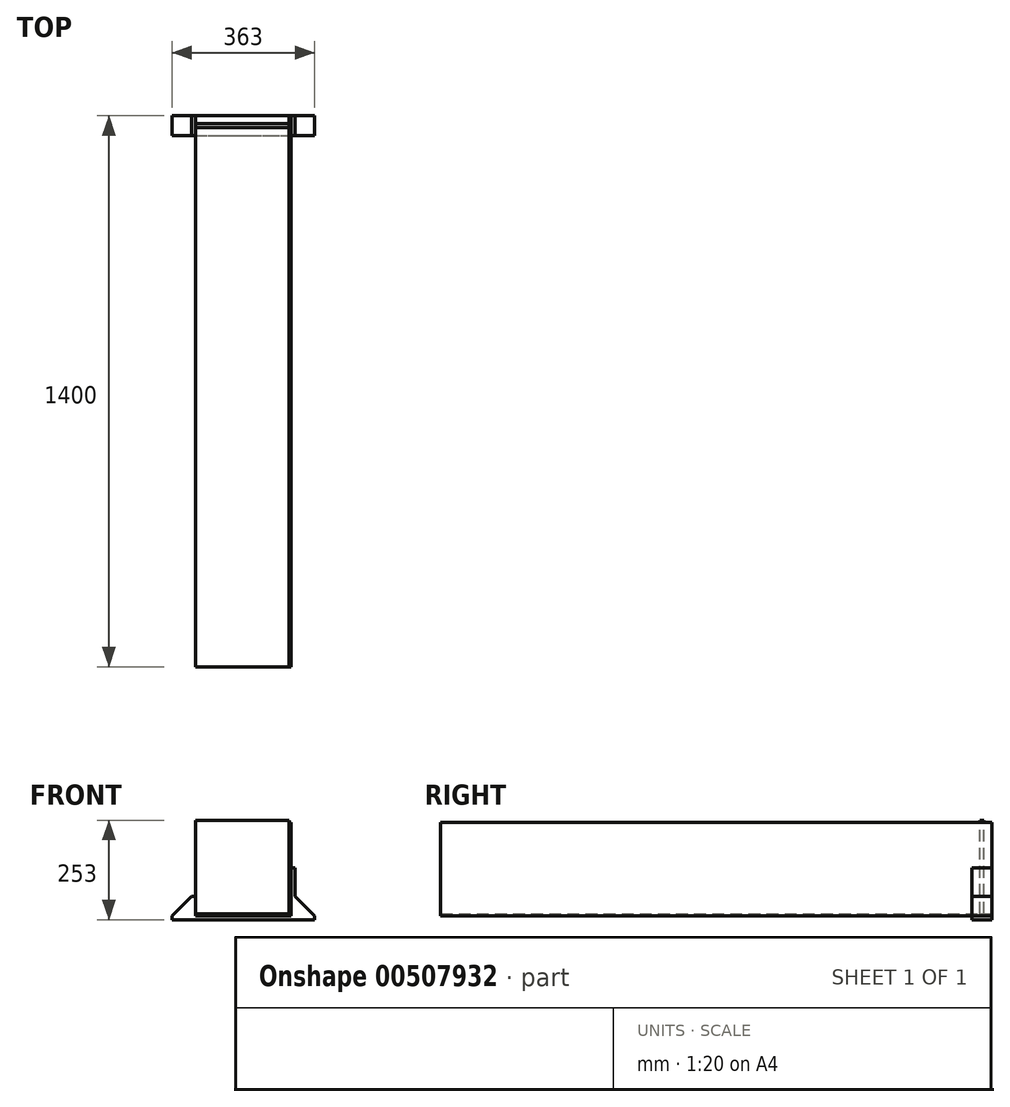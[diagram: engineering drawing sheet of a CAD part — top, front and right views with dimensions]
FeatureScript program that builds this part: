
annotation { "Feature Type Name" : "Feature", "Feature Type Description" : "" }
export const myFeature = defineFeature(function(context is Context, id is Id, definition is map)
    precondition{}
    {
        {
            var Q0;
            Q0=qCreatedBy(makeId("Front.planeOp"),FACE);
            var sketch = newSketch(context, id + "F0", { "sketchPlane" : qUnion([Q0])});
            skLineSegment(sketch, "E0.bottom", {"start": v(-142.05, -154.15) * mm, "end": v(160.95, -154.15) * mm});
            skLineSegment(sketch, "E0.top", {"start": v(-202.05, -164.15) * mm, "end": v(160.95, -164.15) * mm});
            skLineSegment(sketch, "E0.right", {"start": v(160.95, -154.15) * mm, "end": v(160.95, -164.15) * mm});
            skLineSegment(sketch, "E1.bottom", {"start": v(100.95, -32.65) * mm, "end": v(110.95, -32.65) * mm});
            skLineSegment(sketch, "E1.top", {"start": v(100.95, -154.15) * mm, "end": v(110.95, -154.15) * mm});
            skLineSegment(sketch, "E1.left", {"start": v(100.95, -32.65) * mm, "end": v(100.95, -154.15) * mm});
            skLineSegment(sketch, "E1.right", {"start": v(110.95, -32.65) * mm, "end": v(110.95, -154.15) * mm});
            skLineSegment(sketch, "E2", {"start": v(110.95, -104.15) * mm, "end": v(160.95, -154.15) * mm});
            skLineSegment(sketch, "E3", {"start": v(-202.05, -154.15) * mm, "end": v(-202.05, -164.15) * mm});
            skLineSegment(sketch, "E4.bottom", {"start": v(-142.05, -154.15) * mm, "end": v(95.95, -154.15) * mm, "construction": true});
            skLineSegment(sketch, "E4.top", {"start": v(-142.05, -149.15) * mm, "end": v(95.95, -149.15) * mm, "construction": true});
            skLineSegment(sketch, "E4.left", {"start": v(-142.05, -154.15) * mm, "end": v(-142.05, -149.15) * mm, "construction": true});
            skLineSegment(sketch, "E4.right", {"start": v(95.95, -154.15) * mm, "end": v(95.95, -149.15) * mm, "construction": true});
            skLineSegment(sketch, "E5.bottom", {"start": v(100.95, -154.15) * mm, "end": v(100.95, 83.85) * mm, "construction": true});
            skLineSegment(sketch, "E5.top", {"start": v(95.95, -154.15) * mm, "end": v(95.95, 83.85) * mm, "construction": true});
            skLineSegment(sketch, "E5.left", {"start": v(100.95, -154.15) * mm, "end": v(95.95, -154.15) * mm, "construction": true});
            skLineSegment(sketch, "E5.right", {"start": v(100.95, 83.85) * mm, "end": v(95.95, 83.85) * mm, "construction": true});
            skLineSegment(sketch, "E6", {"start": v(-142.05, -154.15) * mm, "end": v(-142.05, -104.15) * mm});
            skLineSegment(sketch, "E7", {"start": v(-142.05, -104.15) * mm, "end": v(-152.05, -104.15) * mm});
            skLineSegment(sketch, "E8", {"start": v(-152.05, -104.15) * mm, "end": v(-152.05, -154.15) * mm});
            skLineSegment(sketch, "E9", {"start": v(-152.05, -154.15) * mm, "end": v(-202.05, -154.15) * mm});
            skLineSegment(sketch, "E10", {"start": v(-202.05, -154.15) * mm, "end": v(-152.05, -104.15) * mm});
            skLineSegment(sketch, "E11", {"start": v(-142.05, -154.15) * mm, "end": v(-152.05, -154.15) * mm});
            skSolve(sketch);
        }
        {
            var Q0;
            Q0 = qSketchRegion(id + "F0", true);
            extrude(context, id + "F1", {"entities" : qUnion([Q0]), "depth" : 50 * mm, "offsetDistance" : 25 * mm});
        }
        {
            var Q0;
            Q0=qCreatedBy(makeId("Front.planeOp"),FACE);
            cPlane(context, id + "F2", {"entities" : qUnion([Q0]), "cplaneType" : CPlaneType.OFFSET, "offset" : 20 * mm, "width" : 150 * mm, "height" : 150 * mm});
        }
        {
            var Q0;
            Q0=qCreatedBy(id+"F2.planeOp",FACE);
            var sketch = newSketch(context, id + "F3", { "sketchPlane" : qUnion([Q0])});
            skLineSegment(sketch, "E12.bottom", {"start": v(-142.05, -149.15) * mm, "end": v(95.95, -149.15) * mm});
            skLineSegment(sketch, "E12.top", {"start": v(-142.05, 88.85) * mm, "end": v(95.95, 88.85) * mm});
            skLineSegment(sketch, "E12.left", {"start": v(-142.05, -149.15) * mm, "end": v(-142.05, 88.85) * mm});
            skLineSegment(sketch, "E12.right", {"start": v(95.95, -149.15) * mm, "end": v(95.95, 88.85) * mm});
            skSolve(sketch);
        }
        {
            var Q0;
            Q0 = qSketchRegion(id + "F3", true);
            extrude(context, id + "F4", {"entities" : qUnion([Q0]), "depth" : 10 * mm, "offsetDistance" : 25 * mm});
        }
        {
            var Q0;
            Q0=qCreatedBy(makeId("Front.planeOp"),FACE);
            var sketch = newSketch(context, id + "F5", { "sketchPlane" : qUnion([Q0])});
            skLineSegment(sketch, "E13.bottom", {"start": v(-142.05, -154.15) * mm, "end": v(95.95, -154.15) * mm});
            skLineSegment(sketch, "E13.top", {"start": v(-142.05, -149.15) * mm, "end": v(95.95, -149.15) * mm});
            skLineSegment(sketch, "E13.left", {"start": v(-142.05, -154.15) * mm, "end": v(-142.05, -149.15) * mm});
            skLineSegment(sketch, "E13.right", {"start": v(95.95, -154.15) * mm, "end": v(95.95, -149.15) * mm});
            skLineSegment(sketch, "E14.bottom", {"start": v(95.95, -154.15) * mm, "end": v(100.95, -154.15) * mm});
            skLineSegment(sketch, "E14.top", {"start": v(95.95, 83.85) * mm, "end": v(100.95, 83.85) * mm});
            skLineSegment(sketch, "E14.left", {"start": v(95.95, -154.15) * mm, "end": v(95.95, 83.85) * mm});
            skLineSegment(sketch, "E14.right", {"start": v(100.95, -154.15) * mm, "end": v(100.95, 83.85) * mm});
            skSolve(sketch);
        }
        {
            var Q0;
            Q0 = qSketchRegion(id + "F5", true);
            extrude(context, id + "F6", {"entities" : qUnion([Q0]), "depth" : 1400 * mm, "offsetDistance" : 25 * mm});
        }
    });
